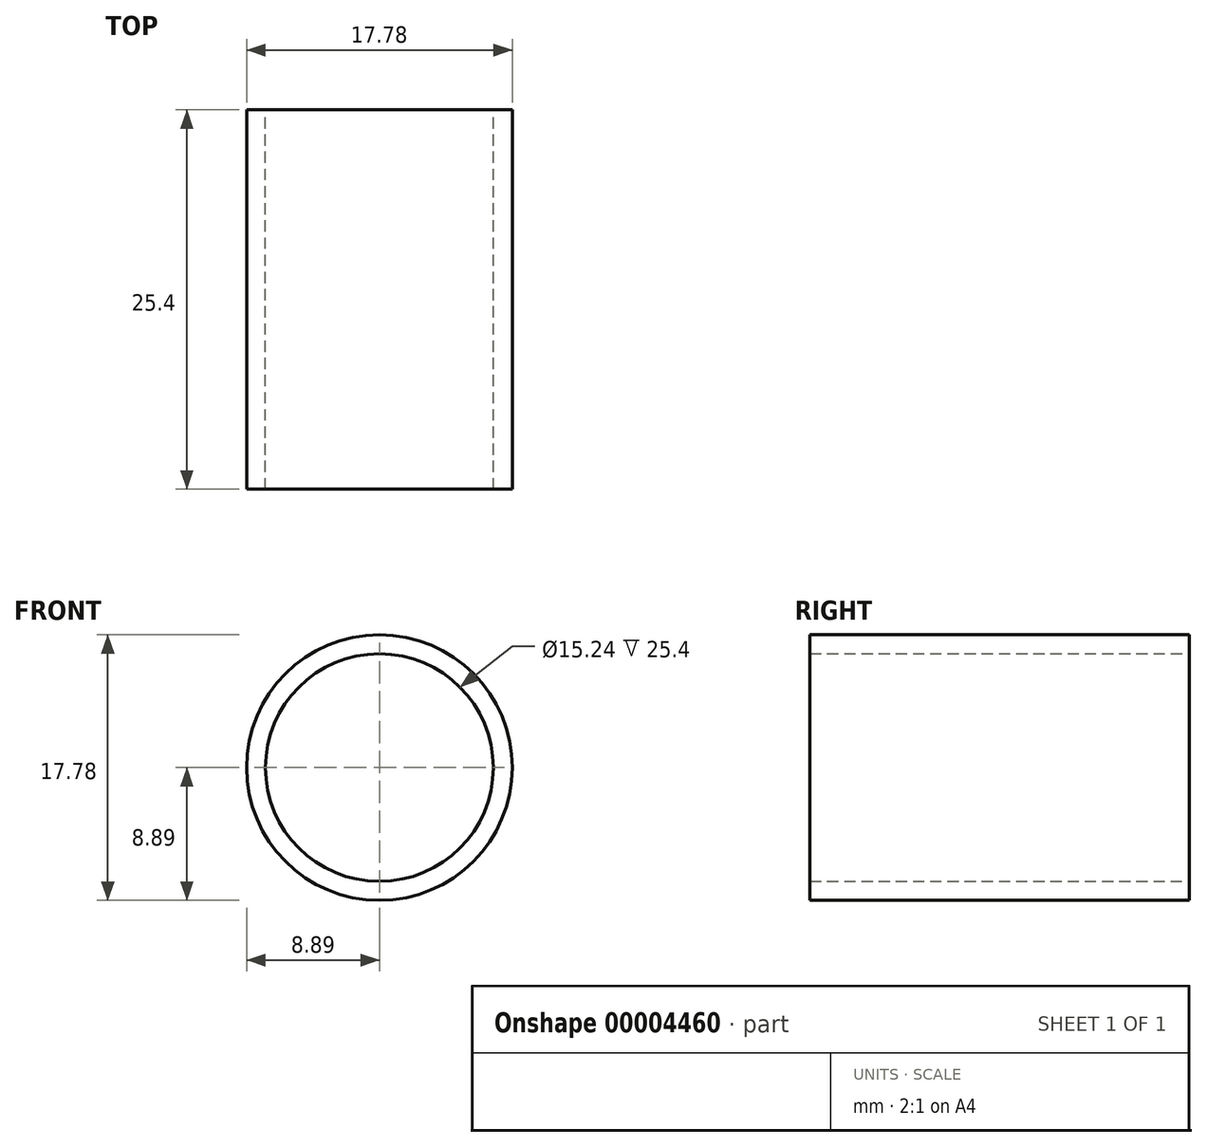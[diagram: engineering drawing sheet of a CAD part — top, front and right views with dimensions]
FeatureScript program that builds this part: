
annotation { "Feature Type Name" : "Feature", "Feature Type Description" : "" }
export const myFeature = defineFeature(function(context is Context, id is Id, definition is map)
    precondition{}
    {
        {
            var Q0;
            Q0=qCreatedBy(makeId("Front.planeOp"),FACE);
            var sketch = newSketch(context, id + "F0", { "sketchPlane" : qUnion([Q0])});
            skCircle(sketch, "E0", {"center": v(0, 0) * mm, "radius": 8.9 * mm});
            skSolve(sketch);
        }
        {
            var Q0;
            Q0 = qSketchRegion(id + "F0", true);
            extrude(context, id + "F1", {"entities" : qUnion([Q0]), "depth" : 25.4 * mm});
        }
        {
            var Q0;
            Q0=makeQuery(id+"F1.opExtrude","CAP_FACE",FACE,{"disambiguationData":[OSD([sQuery(id+"F0.wireOp",EDGE,"E0")])],"isStart":false});
            var sketch = newSketch(context, id + "F2", { "sketchPlane" : qUnion([Q0])});
            skCircle(sketch, "E1", {"center": v(0, 0) * mm, "radius": 8.26 * mm});
            skSolve(sketch);
        }
        {
            var Q0;
            Q0=makeQuery(id+"F2.imprint","IMPRINT",FACE,{"disambiguationData":[TD([[makeQuery(id+"F2.imprint","IMPRINT",EDGE,{"derivedFrom":sQuery(id+"F2.wireOp",EDGE,"E1")}),1.0]])]});
            extrude(context, id + "F3", {"entities" : qUnion([Q0]), "operationType" : NewBodyOperationType.ADD, "oppositeDirection" : true, "depth" : 25.4 * mm});
        }
        {
            var Q0;
            {var subQ0=sQuery(id+"F0.wireOp",EDGE,"E0");Q0=makeQuery(id+"F3.boolean.opBoolean","MERGE",FACE,{"derivedFrom":[makeQuery(id+"F1.opExtrude","CAP_FACE",FACE,{"disambiguationData":[OSD([subQ0])],"isStart":true}),makeQuery(id+"F3.opExtrude","CAP_FACE",FACE,{"disambiguationData":[OSD([subQ0,sQuery(id+"F2.wireOp",EDGE,"E1")])],"isStart":false})]});}
            var sketch = newSketch(context, id + "F4", { "sketchPlane" : qUnion([Q0])});
            skCircle(sketch, "E2", {"center": v(0, 0) * mm, "radius": 12.7 * mm});
            skSolve(sketch);
        }
        {
            var Q0;
            Q0=sQuery(id+"F4.wireOp",VERTEX,"E2.center");
            var Q1;
            Q1=makeQuery(id+"F1.opExtrude","SWEPT_BODY",BODY,{"disambiguationData":[OSD([sQuery(id+"F0.wireOp",EDGE,"E0")])]});
            hole(context, id + "F5", {"style" : HoleStyle.SIMPLE, "holeDiameter" : 15.24 * mm, "endStyle" : HoleEndStyle.THROUGH, "locations" : qUnion([Q0]), "scope" : qUnion([Q1])});
        }
    });
